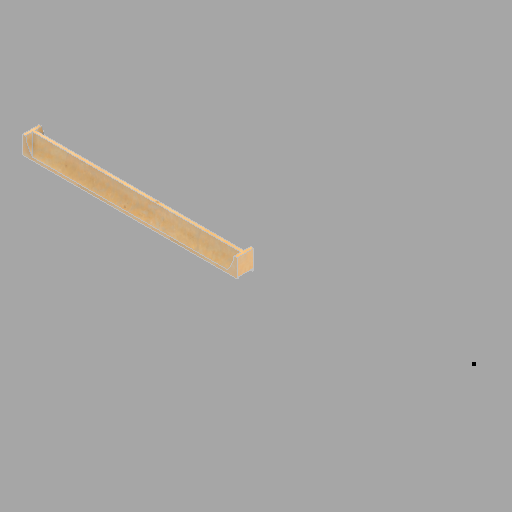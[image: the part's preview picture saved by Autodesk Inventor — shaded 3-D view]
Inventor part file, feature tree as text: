
AUTODESK INVENTOR PART (.ipt)
format: ipt  version: 2022.2 (Build 262287010, 287A)  size: 150,016 bytes
history: native  units: in
note: dims shown in document units (in); Inventor stores cm internally (conversion verified against a paired STEP export)
features: direct_edit x1, sketch x1, revolve x1
ambient origin geometry x8: Origin, YZ Plane, XZ Plane, XY Plane, X Axis, Y Axis, Z Axis, Center Point
bodies: Solid1 (feature_tree), Body1 (feature_tree)
feature tree (3):
  direct_edit  "Direct Edit1"
  sketch  "Sketch1"  dims[d0=180.0deg]
  revolve  "Rotate1"  [1 undecoded]
note: 1 required parameter value undecoded (feature->parameter linkage not recoverable at this tier; creation-order binding heuristic only, values carry confidence <= 0.55)
